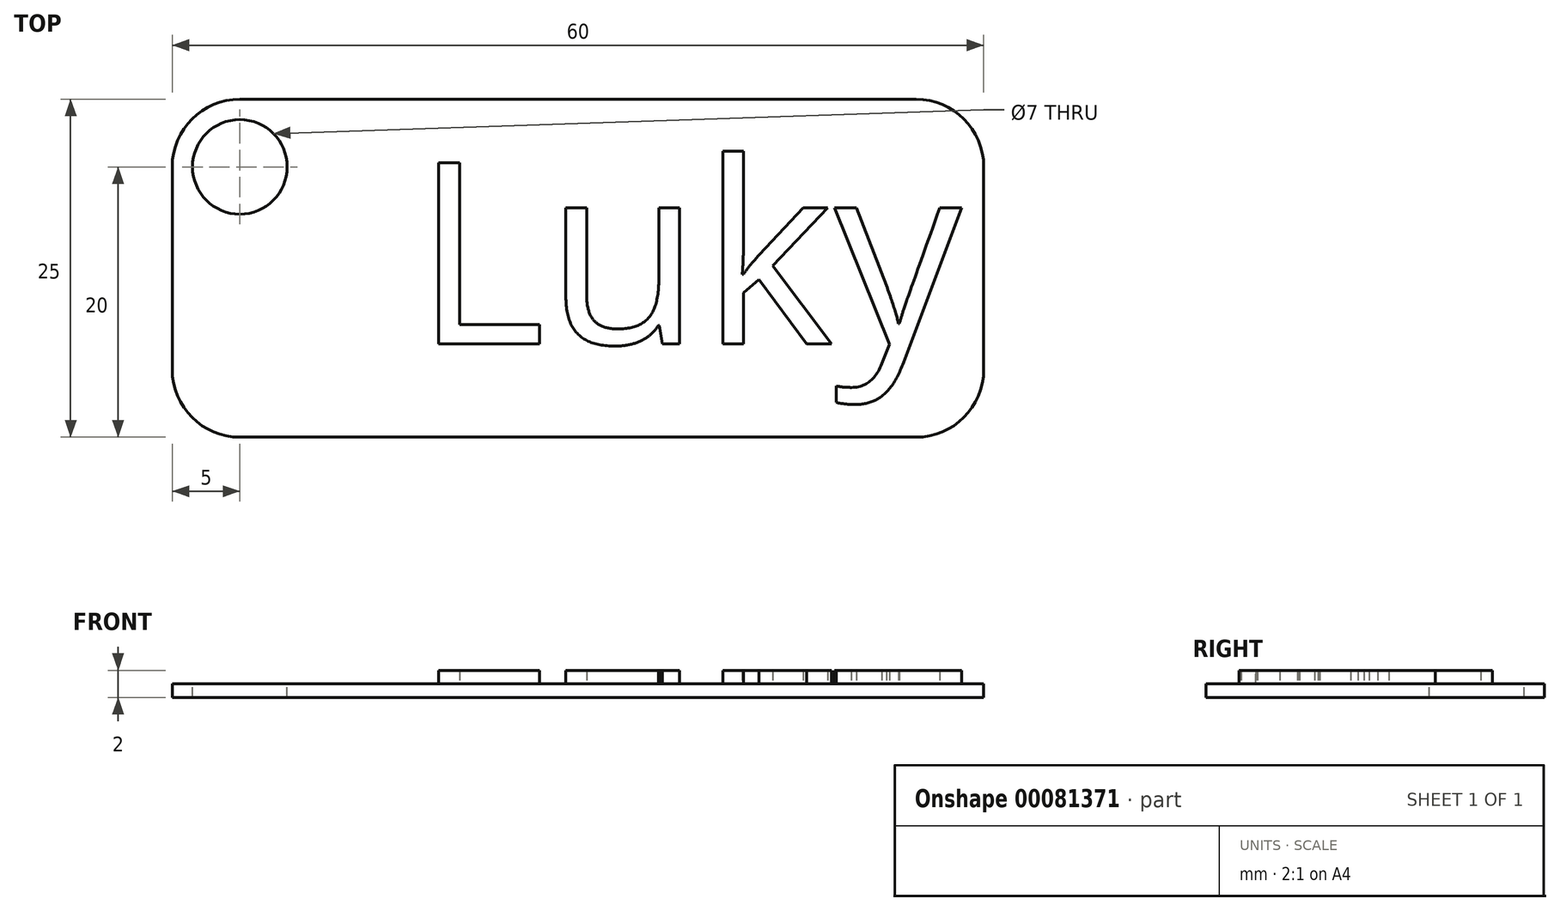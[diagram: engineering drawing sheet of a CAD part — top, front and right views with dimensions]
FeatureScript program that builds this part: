
annotation { "Feature Type Name" : "Feature", "Feature Type Description" : "" }
export const myFeature = defineFeature(function(context is Context, id is Id, definition is map)
    precondition{}
    {
        {
            var Q0;
            Q0=qCreatedBy(makeId("Top.planeOp"),FACE);
            var sketch = newSketch(context, id + "F0", { "sketchPlane" : qUnion([Q0])});
            skLineSegment(sketch, "E0.bottom", {"start": v(-30, -12.5) * mm, "end": v(30, -12.5) * mm});
            skLineSegment(sketch, "E0.top", {"start": v(-30, 12.5) * mm, "end": v(30, 12.5) * mm});
            skLineSegment(sketch, "E0.left", {"start": v(-30, -12.5) * mm, "end": v(-30, 12.5) * mm});
            skLineSegment(sketch, "E0.right", {"start": v(30, -12.5) * mm, "end": v(30, 12.5) * mm});
            skPoint(sketch, "E0.middle", {"position": v(0, 0) * mm});
            skSolve(sketch);
        }
        {
            var Q0;
            Q0 = qSketchRegion(id + "F0", true);
            extrude(context, id + "F1", {"entities" : qUnion([Q0]), "depth" : 1 * mm});
        }
        {
            var Q0;
            Q0=makeQuery(id+"F1.opExtrude","CAP_FACE",FACE,{"disambiguationData":[OSD([sQuery(id+"F0.wireOp",EDGE,"E0.bottom"),sQuery(id+"F0.wireOp",EDGE,"E0.top"),sQuery(id+"F0.wireOp",EDGE,"E0.left"),sQuery(id+"F0.wireOp",EDGE,"E0.right")])],"isStart":false});
            var sketch = newSketch(context, id + "F2", { "sketchPlane" : qUnion([Q0])});
            skText(sketch, "E1", { "text": "Luky\n", "fontName": "OpenSans-Regular.ttf"});
            const initialGuessF2  = {"E1": [-0.01213, -0.00558, 1, 0, 0.0135]};
            skSetInitialGuess(sketch, initialGuessF2);
            skSolve(sketch);
        }
        {
            var Q0;
            Q0 = qSketchRegion(id + "F2", true);
            extrude(context, id + "F3", {"entities" : qUnion([Q0]), "operationType" : NewBodyOperationType.ADD, "depth" : 1 * mm});
        }
        {
            var Q0;
            Q0=makeQuery(id+"F1.opExtrude","SWEPT_EDGE",EDGE,{"disambiguationData":[OSD([sQuery(id+"F0.wireOp",EDGE,"E0.top"),sQuery(id+"F0.wireOp",EDGE,"E0.left")])]});
            var Q1;
            Q1=makeQuery(id+"F1.opExtrude","SWEPT_EDGE",EDGE,{"disambiguationData":[OSD([sQuery(id+"F0.wireOp",EDGE,"E0.bottom"),sQuery(id+"F0.wireOp",EDGE,"E0.left")])]});
            var Q2;
            Q2=makeQuery(id+"F1.opExtrude","SWEPT_EDGE",EDGE,{"disambiguationData":[OSD([sQuery(id+"F0.wireOp",EDGE,"E0.bottom"),sQuery(id+"F0.wireOp",EDGE,"E0.right")])]});
            var Q3;
            Q3=makeQuery(id+"F1.opExtrude","SWEPT_EDGE",EDGE,{"disambiguationData":[OSD([sQuery(id+"F0.wireOp",EDGE,"E0.top"),sQuery(id+"F0.wireOp",EDGE,"E0.right")])]});
            fillet(context, id + "F4", {"entities" : qUnion([Q0, Q1, Q2, Q3]), "radius" : 5 * mm, "tangentPropagation" : true, "allowEdgeOverflow" : false});
        }
        {
            var Q0;
            Q0=makeQuery(id+"F1.opExtrude","CAP_FACE",FACE,{"disambiguationData":[OSD([sQuery(id+"F0.wireOp",EDGE,"E0.bottom"),sQuery(id+"F0.wireOp",EDGE,"E0.top"),sQuery(id+"F0.wireOp",EDGE,"E0.left"),sQuery(id+"F0.wireOp",EDGE,"E0.right")])],"isStart":false});
            var sketch = newSketch(context, id + "F5", { "sketchPlane" : qUnion([Q0])});
            skLineSegment(sketch, "E2", {"start": v(-17.5, 12.5) * mm, "end": v(-17.5, -12.5) * mm, "construction": true});
            skLineSegment(sketch, "E3", {"start": v(-17.5, -12.5) * mm, "end": v(-30, 0) * mm, "construction": true});
            skLineSegment(sketch, "E4", {"start": v(-30, 0) * mm, "end": v(-17.5, 0) * mm, "construction": true});
            skLineSegment(sketch, "E5", {"start": v(-17.5, 0) * mm, "end": v(-28.54, 11.04) * mm, "construction": true});
            skLineSegment(sketch, "E6", {"start": v(-28.54, 11.04) * mm, "end": v(-17.5, 12.5) * mm, "construction": true});
            skLineSegment(sketch, "E7", {"start": v(-30, 0) * mm, "end": v(-28.54, 11.04) * mm, "construction": true});
            skLineSegment(sketch, "E8", {"start": v(-29.19, 6.11) * mm, "end": v(-17.5, 9.98) * mm, "construction": true});
            skPoint(sketch, "E9", {"position": v(-25, 7.5) * mm});
            skSolve(sketch);
        }
        {
            var Q0;
            Q0=sQuery(id+"F5.wireOp",VERTEX,"E9");
            var Q1;
            Q1=makeQuery(id+"F1.opExtrude","SWEPT_BODY",BODY,{"disambiguationData":[OSD([sQuery(id+"F0.wireOp",EDGE,"E0.bottom"),sQuery(id+"F0.wireOp",EDGE,"E0.top"),sQuery(id+"F0.wireOp",EDGE,"E0.left"),sQuery(id+"F0.wireOp",EDGE,"E0.right")])]});
            hole(context, id + "F6", {"style" : HoleStyle.SIMPLE, "endStyle" : HoleEndStyle.BLIND, "holeDiameter" : 7 * mm, "holeDepth" : 50 * mm, "locations" : qUnion([Q0]), "scope" : qUnion([Q1])});
        }
    });
